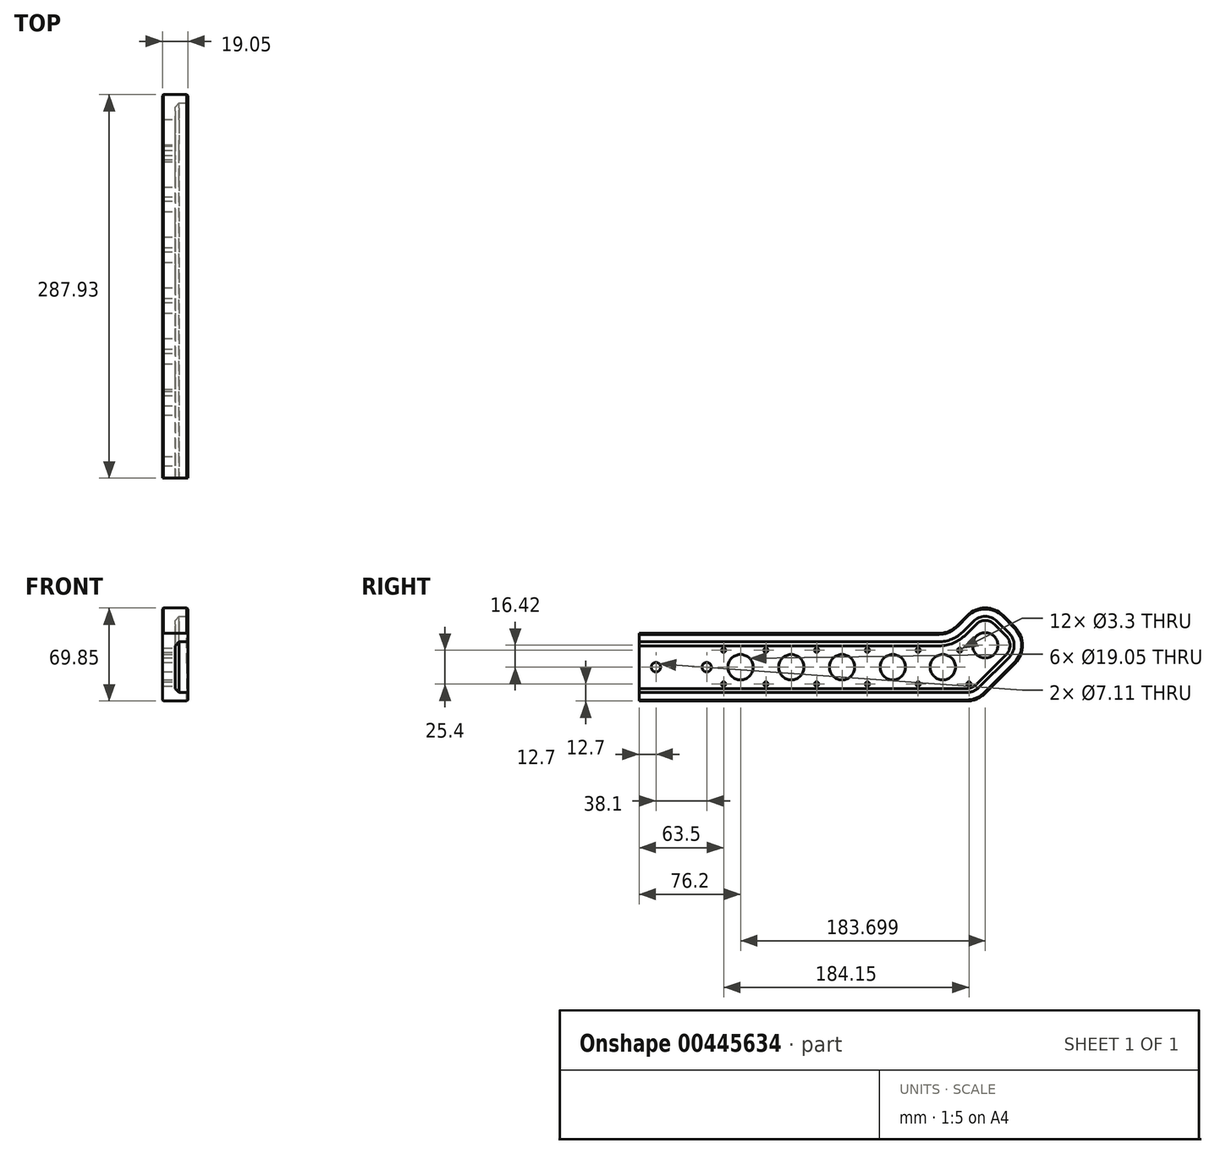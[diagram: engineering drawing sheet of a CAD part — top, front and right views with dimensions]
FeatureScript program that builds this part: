
annotation { "Feature Type Name" : "Feature", "Feature Type Description" : "" }
export const myFeature = defineFeature(function(context is Context, id is Id, definition is map)
    precondition{}
    {
        {
            var Q0;
            Q0=qCreatedBy(makeId("Right.planeOp"),FACE);
            var sketch = newSketch(context, id + "F0", { "sketchPlane" : qUnion([Q0])});
            skLineSegment(sketch, "E0", {"start": v(0, 0) * mm, "end": v(254, 0) * mm});
            skLineSegment(sketch, "E1", {"start": v(254, 0) * mm, "end": v(295.82, 41.82) * mm});
            skLineSegment(sketch, "E2", {"start": v(295.82, 41.82) * mm, "end": v(259.9, 77.74) * mm});
            skLineSegment(sketch, "E3", {"start": v(259.9, 77.74) * mm, "end": v(232.96, 50.8) * mm});
            skLineSegment(sketch, "E4", {"start": v(232.96, 50.8) * mm, "end": v(0, 50.8) * mm});
            skLineSegment(sketch, "E5", {"start": v(0, 50.8) * mm, "end": v(0, 0) * mm});
            skSolve(sketch);
        }
        {
            var Q0;
            Q0 = qSketchRegion(id + "F0", true);
            extrude(context, id + "F1", {"entities" : qUnion([Q0]), "oppositeDirection" : true, "depth" : 19.05 * mm});
        }
        {
            var Q0;
            Q0=makeQuery(id+"F1.opExtrude","SWEPT_EDGE",EDGE,{"disambiguationData":[OSD([sQuery(id+"F0.wireOp",EDGE,"E2"),sQuery(id+"F0.wireOp",EDGE,"E3")])]});
            var Q1;
            Q1=makeQuery(id+"F1.opExtrude","SWEPT_EDGE",EDGE,{"disambiguationData":[OSD([sQuery(id+"F0.wireOp",EDGE,"E1"),sQuery(id+"F0.wireOp",EDGE,"E2")])]});
            var Q2;
            Q2=makeQuery(id+"F1.opExtrude","SWEPT_EDGE",EDGE,{"disambiguationData":[OSD([sQuery(id+"F0.wireOp",EDGE,"E3"),sQuery(id+"F0.wireOp",EDGE,"E4")])]});
            var Q3;
            Q3=makeQuery(id+"F1.opExtrude","SWEPT_EDGE",EDGE,{"disambiguationData":[OSD([sQuery(id+"F0.wireOp",EDGE,"E0"),sQuery(id+"F0.wireOp",EDGE,"E1")])]});
            fillet(context, id + "F2", {"entities" : qUnion([Q0, Q1, Q2, Q3]), "radius" : 19.05 * mm, "tangentPropagation" : true, "allowEdgeOverflow" : false});
        }
        {
            var Q0;
            Q0=makeQuery(id+"F1.opExtrude","CAP_FACE",FACE,{"disambiguationData":[OSD([sQuery(id+"F0.wireOp",EDGE,"E0"),sQuery(id+"F0.wireOp",EDGE,"E1"),sQuery(id+"F0.wireOp",EDGE,"E2"),sQuery(id+"F0.wireOp",EDGE,"E3"),sQuery(id+"F0.wireOp",EDGE,"E4"),sQuery(id+"F0.wireOp",EDGE,"E5")])],"isStart":true});
            var sketch = newSketch(context, id + "F3", { "sketchPlane" : qUnion([Q0])});
            skLineSegment(sketch, "E6.0", {"start": v(225.07, 44.45) * mm, "end": v(0, 44.45) * mm});
            skArc(sketch, "E6.1", {"start": v(243.03, 51.89) * mm, "mid": v(234.79, 46.38) * mm, "end": v(225.07, 44.45) * mm});
            skLineSegment(sketch, "E6.2", {"start": v(250.92, 59.78) * mm, "end": v(243.03, 51.89) * mm});
            skArc(sketch, "E6.3", {"start": v(268.88, 59.78) * mm, "mid": v(259.9, 63.5) * mm, "end": v(250.92, 59.78) * mm});
            skLineSegment(sketch, "E6.4", {"start": v(277.86, 50.8) * mm, "end": v(268.88, 59.78) * mm});
            skLineSegment(sketch, "E6.5", {"start": v(0, 6.35) * mm, "end": v(246.1, 6.35) * mm});
            skArc(sketch, "E6.6", {"start": v(246.1, 6.35) * mm, "mid": v(250.97, 7.32) * mm, "end": v(255.09, 10.07) * mm});
            skLineSegment(sketch, "E6.7", {"start": v(255.09, 10.07) * mm, "end": v(277.86, 32.84) * mm});
            skArc(sketch, "E6.8", {"start": v(277.86, 32.84) * mm, "mid": v(281.58, 41.82) * mm, "end": v(277.86, 50.8) * mm});
            skSolve(sketch);
        }
        {
            var Q0;
            {var subQ0=sQuery(id+"F3.wireOp",EDGE,"E6.0");Q0=makeQuery(id+"F3.imprint","IMPRINT",FACE,{"disambiguationData":[TD([[makeQuery(id+"F3.imprint","IMPRINT",EDGE,{"derivedFrom":subQ0}),1.0]])]});}
            extrude(context, id + "F4", {"entities" : qUnion([Q0]), "operationType" : NewBodyOperationType.REMOVE, "oppositeDirection" : true, "depth" : 9.52 * mm});
        }
        {
            var Q0;
            Q0=makeQuery(id+"F4.boolean.opBoolean","COPY",EDGE,{"derivedFrom":makeQuery(id+"F4.opExtrude","CAP_EDGE",EDGE,{"disambiguationData":[OSD([sQuery(id+"F3.wireOp",EDGE,"E6.0")])],"isStart":false})});
            chamfer(context, id + "F5", {"entities" : qUnion([Q0]), "width" : 3.05 * mm, "tangentPropagation" : true});
        }
        {
            var Q0;
            Q0=makeQuery(id+"F4.boolean.opBoolean","COPY",FACE,{"derivedFrom":makeQuery(id+"F4.opExtrude","CAP_FACE",FACE,{"disambiguationData":[OSD([sQuery(id+"F0.wireOp",EDGE,"E5"),sQuery(id+"F3.wireOp",EDGE,"E6.0"),sQuery(id+"F3.wireOp",EDGE,"E6.1"),sQuery(id+"F3.wireOp",EDGE,"E6.2"),sQuery(id+"F3.wireOp",EDGE,"E6.3"),sQuery(id+"F3.wireOp",EDGE,"E6.4"),sQuery(id+"F3.wireOp",EDGE,"E6.5"),sQuery(id+"F3.wireOp",EDGE,"E6.6"),sQuery(id+"F3.wireOp",EDGE,"E6.7"),sQuery(id+"F3.wireOp",EDGE,"E6.8")])],"isStart":false})});
            var sketch = newSketch(context, id + "F6", { "sketchPlane" : qUnion([Q0])});
            skCircle(sketch, "E7", {"center": v(76.2, 25.4) * mm, "radius": 9.53 * mm});
            skCircle(sketch, "E8", {"center": v(114.3, 25.4) * mm, "radius": 9.53 * mm});
            skCircle(sketch, "E9", {"center": v(152.4, 25.4) * mm, "radius": 9.53 * mm});
            skCircle(sketch, "E10", {"center": v(259.9, 41.82) * mm, "radius": 9.53 * mm});
            skCircle(sketch, "E11", {"center": v(190.5, 25.4) * mm, "radius": 9.53 * mm});
            skCircle(sketch, "E12", {"center": v(228.01, 25.4) * mm, "radius": 9.53 * mm});
            skSolve(sketch);
        }
        {
            var Q0;
            Q0 = qSketchRegion(id + "F6", true);
            extrude(context, id + "F7", {"entities" : qUnion([Q0]), "operationType" : NewBodyOperationType.REMOVE, "endBound" : BoundingType.THROUGH_ALL, "oppositeDirection" : true, "depth" : 25.4 * mm});
        }
        {
            var Q0;
            Q0=makeQuery(id+"F7.boolean.opBoolean","COPY",EDGE,{"derivedFrom":makeQuery(id+"F7.opExtrude","CAP_EDGE",EDGE,{"disambiguationData":[OSD([sQuery(id+"F6.wireOp",EDGE,"E7")])],"isStart":true})});
            var Q1;
            Q1=makeQuery(id+"F7.boolean.opBoolean","COPY",EDGE,{"derivedFrom":makeQuery(id+"F7.opExtrude","CAP_EDGE",EDGE,{"disambiguationData":[OSD([sQuery(id+"F6.wireOp",EDGE,"E8")])],"isStart":true})});
            var Q2;
            Q2=makeQuery(id+"F7.boolean.opBoolean","COPY",EDGE,{"derivedFrom":makeQuery(id+"F7.opExtrude","CAP_EDGE",EDGE,{"disambiguationData":[OSD([sQuery(id+"F6.wireOp",EDGE,"E9")])],"isStart":true})});
            var Q3;
            Q3=makeQuery(id+"F7.boolean.opBoolean","COPY",EDGE,{"derivedFrom":makeQuery(id+"F7.opExtrude","CAP_EDGE",EDGE,{"disambiguationData":[OSD([sQuery(id+"F6.wireOp",EDGE,"E11")])],"isStart":true})});
            var Q4;
            Q4=makeQuery(id+"F7.boolean.opBoolean","COPY",EDGE,{"derivedFrom":makeQuery(id+"F7.opExtrude","CAP_EDGE",EDGE,{"disambiguationData":[OSD([sQuery(id+"F6.wireOp",EDGE,"E12")])],"isStart":true})});
            var Q5;
            Q5=makeQuery(id+"F7.boolean.opBoolean","COPY",EDGE,{"derivedFrom":makeQuery(id+"F7.opExtrude","CAP_EDGE",EDGE,{"disambiguationData":[OSD([sQuery(id+"F6.wireOp",EDGE,"E10")])],"isStart":true})});
            var Q6;
            Q6=makeQuery(id+"F1.opExtrude","CAP_EDGE",EDGE,{"disambiguationData":[OSD([sQuery(id+"F0.wireOp",EDGE,"E0")])],"isStart":true});
            var Q7;
            Q7=makeQuery(id+"F4.boolean.opBoolean","COPY",EDGE,{"derivedFrom":makeQuery(id+"F4.opExtrude","CAP_EDGE",EDGE,{"disambiguationData":[OSD([sQuery(id+"F3.wireOp",EDGE,"E6.7")])],"isStart":true})});
            var Q8;
            Q8=makeQuery(id+"F1.opExtrude","CAP_EDGE",EDGE,{"disambiguationData":[OSD([sQuery(id+"F0.wireOp",EDGE,"E0")])],"isStart":false});
            chamfer(context, id + "F8", {"entities" : qUnion([Q0, Q1, Q2, Q3, Q4, Q5, Q6, Q7, Q8]), "width" : 0.76 * mm, "tangentPropagation" : true});
        }
        {
            var Q0;
            Q0=makeQuery(id+"F4.boolean.opBoolean","COPY",FACE,{"derivedFrom":makeQuery(id+"F4.opExtrude","CAP_FACE",FACE,{"disambiguationData":[OSD([sQuery(id+"F0.wireOp",EDGE,"E5"),sQuery(id+"F3.wireOp",EDGE,"E6.0"),sQuery(id+"F3.wireOp",EDGE,"E6.1"),sQuery(id+"F3.wireOp",EDGE,"E6.2"),sQuery(id+"F3.wireOp",EDGE,"E6.3"),sQuery(id+"F3.wireOp",EDGE,"E6.4"),sQuery(id+"F3.wireOp",EDGE,"E6.5"),sQuery(id+"F3.wireOp",EDGE,"E6.6"),sQuery(id+"F3.wireOp",EDGE,"E6.7"),sQuery(id+"F3.wireOp",EDGE,"E6.8")])],"isStart":false})});
            var sketch = newSketch(context, id + "F9", { "sketchPlane" : qUnion([Q0])});
            skPoint(sketch, "E13", {"position": v(12.7, 25.4) * mm});
            skPoint(sketch, "E14", {"position": v(50.8, 25.4) * mm});
            skSolve(sketch);
        }
        {
            var Q0;
            Q0=sQuery(id+"F9.wireOp",VERTEX,"E14");
            var Q1;
            Q1=sQuery(id+"F9.wireOp",VERTEX,"E13");
            var Q2;
            Q2=makeQuery(id+"F1.opExtrude","SWEPT_BODY",BODY,{"disambiguationData":[OSD([sQuery(id+"F0.wireOp",EDGE,"E0"),sQuery(id+"F0.wireOp",EDGE,"E1"),sQuery(id+"F0.wireOp",EDGE,"E2"),sQuery(id+"F0.wireOp",EDGE,"E3"),sQuery(id+"F0.wireOp",EDGE,"E4"),sQuery(id+"F0.wireOp",EDGE,"E5")])]});
            hole(context, id + "F10", {"style" : HoleStyle.SIMPLE, "endStyle" : HoleEndStyle.THROUGH, "holeDiameter" : 7.11 * mm, "isTappedThrough" : true, "tappedDepth" : 12.7 * mm, "tapClearance" : 3, "locations" : qUnion([Q0, Q1]), "scope" : qUnion([Q2])});
        }
        {
            var Q0;
            Q0=makeQuery(id+"F4.boolean.opBoolean","COPY",FACE,{"derivedFrom":makeQuery(id+"F4.opExtrude","CAP_FACE",FACE,{"disambiguationData":[OSD([sQuery(id+"F0.wireOp",EDGE,"E5"),sQuery(id+"F3.wireOp",EDGE,"E6.0"),sQuery(id+"F3.wireOp",EDGE,"E6.1"),sQuery(id+"F3.wireOp",EDGE,"E6.2"),sQuery(id+"F3.wireOp",EDGE,"E6.3"),sQuery(id+"F3.wireOp",EDGE,"E6.4"),sQuery(id+"F3.wireOp",EDGE,"E6.5"),sQuery(id+"F3.wireOp",EDGE,"E6.6"),sQuery(id+"F3.wireOp",EDGE,"E6.7"),sQuery(id+"F3.wireOp",EDGE,"E6.8")])],"isStart":false})});
            var sketch = newSketch(context, id + "F11", { "sketchPlane" : qUnion([Q0])});
            skPoint(sketch, "E15", {"position": v(63.5, 12.7) * mm});
            skPoint(sketch, "E16", {"position": v(95.25, 12.7) * mm});
            skPoint(sketch, "E17", {"position": v(133.35, 12.7) * mm});
            skPoint(sketch, "E18", {"position": v(171.45, 12.7) * mm});
            skPoint(sketch, "E19", {"position": v(209.55, 12.7) * mm});
            skPoint(sketch, "E20", {"position": v(247.65, 12.7) * mm});
            skPoint(sketch, "E21", {"position": v(63.5, 38.1) * mm});
            skPoint(sketch, "E22", {"position": v(95.25, 38.1) * mm});
            skPoint(sketch, "E23", {"position": v(133.35, 38.1) * mm});
            skPoint(sketch, "E24", {"position": v(171.45, 38.1) * mm});
            skPoint(sketch, "E25", {"position": v(209.55, 38.1) * mm});
            skPoint(sketch, "E26", {"position": v(240.71, 38.1) * mm});
            skCircle(sketch, "E27.0", {"center": v(76.2, 25.4) * mm, "radius": 9.53 * mm});
            skCircle(sketch, "E28.0", {"center": v(259.9, 41.82) * mm, "radius": 10.29 * mm});
            skCircle(sketch, "E29.0", {"center": v(228.01, 25.4) * mm, "radius": 9.53 * mm});
            skSolve(sketch);
        }
        {
            var Q0;
            Q0=sQuery(id+"F11.wireOp",VERTEX,"E20");
            var Q1;
            Q1=sQuery(id+"F11.wireOp",VERTEX,"E26");
            var Q2;
            Q2=sQuery(id+"F11.wireOp",VERTEX,"E19");
            var Q3;
            Q3=sQuery(id+"F11.wireOp",VERTEX,"E25");
            var Q4;
            Q4=sQuery(id+"F11.wireOp",VERTEX,"E18");
            var Q5;
            Q5=sQuery(id+"F11.wireOp",VERTEX,"E24");
            var Q6;
            Q6=sQuery(id+"F11.wireOp",VERTEX,"E17");
            var Q7;
            Q7=sQuery(id+"F11.wireOp",VERTEX,"E23");
            var Q8;
            Q8=sQuery(id+"F11.wireOp",VERTEX,"E16");
            var Q9;
            Q9=sQuery(id+"F11.wireOp",VERTEX,"E22");
            var Q10;
            Q10=sQuery(id+"F11.wireOp",VERTEX,"E15");
            var Q11;
            Q11=sQuery(id+"F11.wireOp",VERTEX,"E21");
            var Q12;
            Q12=makeQuery(id+"F1.opExtrude","SWEPT_BODY",BODY,{"disambiguationData":[OSD([sQuery(id+"F0.wireOp",EDGE,"E0"),sQuery(id+"F0.wireOp",EDGE,"E1"),sQuery(id+"F0.wireOp",EDGE,"E2"),sQuery(id+"F0.wireOp",EDGE,"E3"),sQuery(id+"F0.wireOp",EDGE,"E4"),sQuery(id+"F0.wireOp",EDGE,"E5")])]});
            hole(context, id + "F12", {"style" : HoleStyle.SIMPLE, "endStyle" : HoleEndStyle.THROUGH, "holeDiameter" : 3.3 * mm, "isTappedThrough" : true, "tappedDepth" : 12.7 * mm, "tapClearance" : 3, "locations" : qUnion([Q0, Q1, Q2, Q3, Q4, Q5, Q6, Q7, Q8, Q9, Q10, Q11]), "scope" : qUnion([Q12])});
        }
    });
